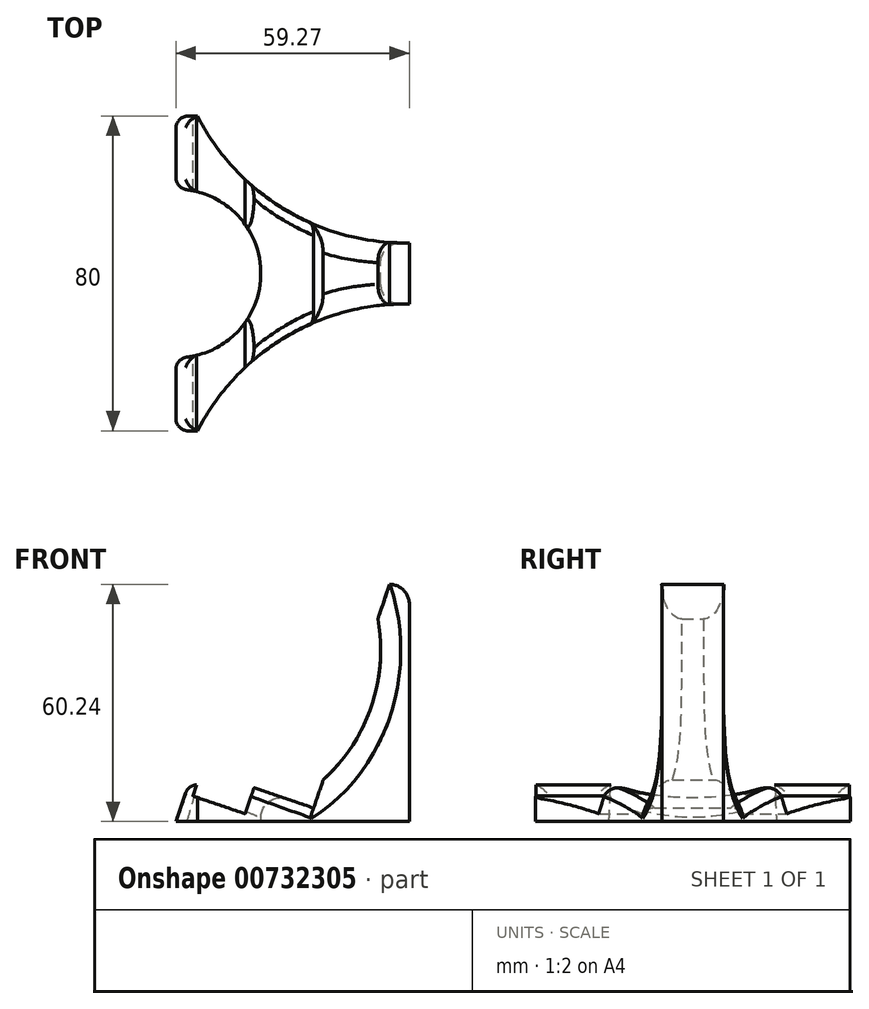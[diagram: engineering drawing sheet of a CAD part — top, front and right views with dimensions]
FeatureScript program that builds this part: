
annotation { "Feature Type Name" : "Feature", "Feature Type Description" : "" }
export const myFeature = defineFeature(function(context is Context, id is Id, definition is map)
    precondition{}
    {
        {
            var Q0;
            Q0=qCreatedBy(makeId("Front.planeOp"),FACE);
            var sketch = newSketch(context, id + "F0", { "sketchPlane" : qUnion([Q0])});
            skLineSegment(sketch, "E0", {"start": v(0, 0) * mm, "end": v(-13.26, 4.5) * mm});
            skLineSegment(sketch, "E1", {"start": v(-13.26, 4.5) * mm, "end": v(-12.3, 7.35) * mm});
            skLineSegment(sketch, "E2", {"start": v(-12.3, 7.35) * mm, "end": v(-14.18, 7.99) * mm});
            skLineSegment(sketch, "E3", {"start": v(-14.18, 7.99) * mm, "end": v(-17.56, -1.95) * mm});
            skLineSegment(sketch, "E4", {"start": v(0, 0) * mm, "end": v(2.25, 6.63) * mm});
            skLineSegment(sketch, "E5", {"start": v(2.25, 6.63) * mm, "end": v(17.4, 1.48) * mm});
            skLineSegment(sketch, "E6", {"start": v(17.4, 1.48) * mm, "end": v(36.7, 58.29) * mm});
            skLineSegment(sketch, "E7", {"start": v(36.7, 58.29) * mm, "end": v(41.7, 58.29) * mm});
            skLineSegment(sketch, "E8", {"start": v(41.7, 58.29) * mm, "end": v(41.7, -1.95) * mm});
            skLineSegment(sketch, "E9", {"start": v(41.7, -1.95) * mm, "end": v(-17.56, -1.95) * mm});
            skSolve(sketch);
        }
        {
            var Q0;
            Q0 = qSketchRegion(id + "F0", true);
            extrude(context, id + "F1", {"entities" : qUnion([Q0]), "depth" : 80 * mm, "offsetDistance" : 25 * mm});
        }
        {
            var Q0;
            Q0=makeQuery(id+"F1.opExtrude","SWEPT_FACE",FACE,{"disambiguationData":[OSD([sQuery(id+"F0.wireOp",EDGE,"E7")])]});
            var sketch = newSketch(context, id + "F2", { "sketchPlane" : qUnion([Q0])});
            skLineSegment(sketch, "E10", {"start": v(41.7, -40) * mm, "end": v(-49.98, -40) * mm, "construction": true});
            skArc(sketch, "E11", {"start": v(-12.14, 0) * mm, "mid": v(10.18, -23.8) * mm, "end": v(41.7, -32.24) * mm});
            skLineSegment(sketch, "E12", {"start": v(-12.14, 0) * mm, "end": v(41.7, 0) * mm});
            skLineSegment(sketch, "E13", {"start": v(41.7, 0) * mm, "end": v(41.7, -32.24) * mm});
            skArc(sketch, "E14.MirrorCS", {"start": v(-12.14, -80) * mm, "mid": v(10.18, -56.2) * mm, "end": v(41.7, -47.76) * mm});
            skLineSegment(sketch, "E15.MirrorCS", {"start": v(-12.14, -80) * mm, "end": v(41.7, -80) * mm});
            skLineSegment(sketch, "E16.MirrorCS", {"start": v(41.7, -80) * mm, "end": v(41.7, -47.76) * mm});
            skCircle(sketch, "E17", {"center": v(-17.43, -40) * mm, "radius": 21.42 * mm});
            skSolve(sketch);
        }
        {
            var Q0;
            Q0 = qSketchRegion(id + "F2", true);
            extrude(context, id + "F3", {"entities" : qUnion([Q0]), "operationType" : NewBodyOperationType.REMOVE, "endBound" : BoundingType.THROUGH_ALL, "oppositeDirection" : true, "depth" : 25 * mm, "offsetDistance" : 25 * mm});
        }
        {
            var Q0;
            Q0=qCreatedBy(makeId("Front.planeOp"),FACE);
            var sketch = newSketch(context, id + "F4", { "sketchPlane" : qUnion([Q0])});
            skArc(sketch, "E18", {"start": v(19.26, 8.15) * mm, "mid": v(32, 27.08) * mm, "end": v(33.65, 49.83) * mm});
            skLineSegment(sketch, "E19", {"start": v(33.65, 49.83) * mm, "end": v(19.26, 8.15) * mm});
            skSolve(sketch);
        }
        {
            var Q0;
            Q0 = qSketchRegion(id + "F4", true);
            extrude(context, id + "F5", {"entities" : qUnion([Q0]), "operationType" : NewBodyOperationType.REMOVE, "endBound" : BoundingType.THROUGH_ALL, "depth" : 25 * mm, "offsetDistance" : 25 * mm});
        }
        {
            var Q0;
            {var subQ0=sQuery(id+"F0.wireOp",EDGE,"E3");var subQ1=sQuery(id+"F0.wireOp",EDGE,"E2");Q0=makeQuery(id+"F3.boolean.opBoolean","SPLIT",EDGE,{"disambiguationData":[TD([makeQuery(id+"F1.opExtrude","CAP_FACE",FACE,{"disambiguationData":[OSD([sQuery(id+"F0.wireOp",EDGE,"E0"),sQuery(id+"F0.wireOp",EDGE,"E1"),subQ1,subQ0,sQuery(id+"F0.wireOp",EDGE,"E4"),sQuery(id+"F0.wireOp",EDGE,"E5"),sQuery(id+"F0.wireOp",EDGE,"E6"),sQuery(id+"F0.wireOp",EDGE,"E7"),sQuery(id+"F0.wireOp",EDGE,"E8"),sQuery(id+"F0.wireOp",EDGE,"E9")])],"isStart":true})])],"derivedFrom":makeQuery(id+"F1.opExtrude","SWEPT_EDGE",EDGE,{"disambiguationData":[OSD([subQ1,subQ0])]})});}
            var Q1;
            {var subQ0=sQuery(id+"F0.wireOp",EDGE,"E3");var subQ1=sQuery(id+"F0.wireOp",EDGE,"E2");Q1=makeQuery(id+"F3.boolean.opBoolean","SPLIT",EDGE,{"disambiguationData":[TD([makeQuery(id+"F1.opExtrude","CAP_FACE",FACE,{"disambiguationData":[OSD([sQuery(id+"F0.wireOp",EDGE,"E0"),sQuery(id+"F0.wireOp",EDGE,"E1"),subQ1,subQ0,sQuery(id+"F0.wireOp",EDGE,"E4"),sQuery(id+"F0.wireOp",EDGE,"E5"),sQuery(id+"F0.wireOp",EDGE,"E6"),sQuery(id+"F0.wireOp",EDGE,"E7"),sQuery(id+"F0.wireOp",EDGE,"E8"),sQuery(id+"F0.wireOp",EDGE,"E9")])],"isStart":false})])],"derivedFrom":makeQuery(id+"F1.opExtrude","SWEPT_EDGE",EDGE,{"disambiguationData":[OSD([subQ1,subQ0])]})});}
            var Q2;
            Q2=makeQuery(id+"F1.opExtrude","CAP_EDGE",EDGE,{"disambiguationData":[OSD([sQuery(id+"F0.wireOp",EDGE,"E3")])],"isStart":false});
            var Q3;
            Q3=makeQuery(id+"F3.boolean.opBoolean","INTERSECT",EDGE,{"disambiguationData":[OD(1.0)],"derivedFrom":[makeQuery(id+"F1.opExtrude","SWEPT_FACE",FACE,{"disambiguationData":[OSD([sQuery(id+"F0.wireOp",EDGE,"E3")])]}),makeQuery(id+"F3.opExtrude","SWEPT_FACE",FACE,{"disambiguationData":[OSD([sQuery(id+"F2.wireOp",EDGE,"E17")])]})]});
            var Q4;
            Q4=makeQuery(id+"F3.boolean.opBoolean","INTERSECT",EDGE,{"disambiguationData":[OD(0.0)],"derivedFrom":[makeQuery(id+"F1.opExtrude","SWEPT_FACE",FACE,{"disambiguationData":[OSD([sQuery(id+"F0.wireOp",EDGE,"E3")])]}),makeQuery(id+"F3.opExtrude","SWEPT_FACE",FACE,{"disambiguationData":[OSD([sQuery(id+"F2.wireOp",EDGE,"E17")])]})]});
            var Q5;
            Q5=makeQuery(id+"F1.opExtrude","CAP_EDGE",EDGE,{"disambiguationData":[OSD([sQuery(id+"F0.wireOp",EDGE,"E3")])],"isStart":true});
            fillet(context, id + "F6", {"entities" : qUnion([Q0, Q1, Q2, Q3, Q4, Q5]), "radius" : 3 * mm, "tangentPropagation" : true, "allowEdgeOverflow" : false});
        }
        {
            var Q0;
            Q0=makeQuery(id+"F3.boolean.opBoolean","COPY",EDGE,{"derivedFrom":makeQuery(id+"F3.opExtrude","SWEPT_EDGE",EDGE,{"disambiguationData":[OSD([sQuery(id+"F0.wireOp",EDGE,"E7"),sQuery(id+"F0.wireOp",EDGE,"E8"),sQuery(id+"F2.wireOp",EDGE,"E11"),sQuery(id+"F2.wireOp",EDGE,"E13")])]})});
            var Q1;
            Q1=makeQuery(id+"F3.boolean.opBoolean","COPY",EDGE,{"derivedFrom":makeQuery(id+"F3.opExtrude","SWEPT_EDGE",EDGE,{"disambiguationData":[OSD([sQuery(id+"F0.wireOp",EDGE,"E7"),sQuery(id+"F0.wireOp",EDGE,"E8"),sQuery(id+"F2.wireOp",EDGE,"E14.MirrorCS"),sQuery(id+"F2.wireOp",EDGE,"E16.MirrorCS")])]})});
            var Q2;
            Q2=makeQuery(id+"F1.opExtrude","SWEPT_EDGE",EDGE,{"disambiguationData":[OSD([sQuery(id+"F0.wireOp",EDGE,"E7"),sQuery(id+"F0.wireOp",EDGE,"E8")])]});
            fillet(context, id + "F7", {"entities" : qUnion([Q0, Q1, Q2]), "radius" : 5 * mm, "tangentPropagation" : true, "allowEdgeOverflow" : false});
        }
        {
            var Q0;
            Q0=makeQuery(id+"F5.boolean.opBoolean","INTERSECT",EDGE,{"derivedFrom":[makeQuery(id+"F3.boolean.opBoolean","COPY",FACE,{"derivedFrom":makeQuery(id+"F3.opExtrude","SWEPT_FACE",FACE,{"disambiguationData":[OSD([sQuery(id+"F2.wireOp",EDGE,"E14.MirrorCS")])]})}),makeQuery(id+"F5.opExtrude","SWEPT_FACE",FACE,{"disambiguationData":[OSD([sQuery(id+"F4.wireOp",EDGE,"E18")])]})]});
            var Q1;
            Q1=makeQuery(id+"F5.boolean.opBoolean","INTERSECT",EDGE,{"derivedFrom":[makeQuery(id+"F3.boolean.opBoolean","COPY",FACE,{"derivedFrom":makeQuery(id+"F3.opExtrude","SWEPT_FACE",FACE,{"disambiguationData":[OSD([sQuery(id+"F2.wireOp",EDGE,"E11")])]})}),makeQuery(id+"F5.opExtrude","SWEPT_FACE",FACE,{"disambiguationData":[OSD([sQuery(id+"F4.wireOp",EDGE,"E18")])]})]});
            fillet(context, id + "F8", {"entities" : qUnion([Q0, Q1]), "radius" : 5 * mm, "tangentPropagation" : true, "allowEdgeOverflow" : false});
        }
        {
            var Q0;
            Q0=makeQuery(id+"F3.boolean.opBoolean","INTERSECT",EDGE,{"derivedFrom":[makeQuery(id+"F1.opExtrude","SWEPT_FACE",FACE,{"disambiguationData":[OSD([sQuery(id+"F0.wireOp",EDGE,"E5")])]}),makeQuery(id+"F3.opExtrude","SWEPT_FACE",FACE,{"disambiguationData":[OSD([sQuery(id+"F2.wireOp",EDGE,"E14.MirrorCS")])]})]});
            var Q1;
            Q1=makeQuery(id+"F3.boolean.opBoolean","INTERSECT",EDGE,{"derivedFrom":[makeQuery(id+"F1.opExtrude","SWEPT_FACE",FACE,{"disambiguationData":[OSD([sQuery(id+"F0.wireOp",EDGE,"E5")])]}),makeQuery(id+"F3.opExtrude","SWEPT_FACE",FACE,{"disambiguationData":[OSD([sQuery(id+"F2.wireOp",EDGE,"E11")])]})]});
            fillet(context, id + "F9", {"entities" : qUnion([Q0, Q1]), "radius" : 3 * mm, "tangentPropagation" : true, "allowEdgeOverflow" : false});
        }
        {
            var Q0;
            Q0=makeQuery(id+"F3.boolean.opBoolean","INTERSECT",EDGE,{"derivedFrom":[makeQuery(id+"F1.opExtrude","SWEPT_FACE",FACE,{"disambiguationData":[OSD([sQuery(id+"F0.wireOp",EDGE,"E5")])]}),makeQuery(id+"F3.opExtrude","SWEPT_FACE",FACE,{"disambiguationData":[OSD([sQuery(id+"F2.wireOp",EDGE,"E17")])]})]});
            fillet(context, id + "F10", {"entities" : qUnion([Q0]), "radius" : 5 * mm, "tangentPropagation" : true, "allowEdgeOverflow" : false});
        }
    });
